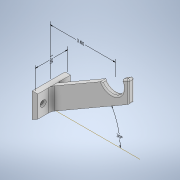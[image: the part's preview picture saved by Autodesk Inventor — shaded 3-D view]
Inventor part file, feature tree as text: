
AUTODESK INVENTOR PART (.ipt)
format: ipt  version: 2021.1 (Build 251245010, 245A)  size: 431,104 bytes
history: native  units: in
note: dims shown in document units (in); Inventor stores cm internally (conversion verified against a paired STEP export)
features: sketch x5, other x4, extrude x4, fillet x4, hole x1
ambient origin geometry x8: Origin, YZ Plane, XZ Plane, XY Plane, X Axis, Y Axis, Z Axis, Center Point
bodies: Solid2 (feature_tree)
feature tree (18):
  other  "Annotations"
  extrude  "Extrusion3"  Depth=0.25in
  extrude  "Extrusion4"  TaperAngle=30.0deg  [1 undecoded]
  sketch  "Sketch7"  dims[d26=1.075in d29=0.25in]
  extrude  "Extrusion5"  Depth=0.25in
  hole  "Hole3"  [1 undecoded]
  fillet  "Fillet3"  [1 undecoded]
  fillet  "Fillet4"  [1 undecoded]
  fillet  "Fillet5"  Radius=0.25in
  fillet  "Fillet6"  Radius=0.25in
  extrude  "Extrusion6"  Depth=0.0625in
  sketch  "Sketch5"  dims[d21=1.0in d22=0.25in]
  sketch  "Sketch6"  dims[d23=1.5in d24=0.0in d25=30.0deg]
  sketch  "Sketch8"  dims[d30=3.0in d31=0.25in d32=0.0in d33=0.0in d34=0.25in d35=0.25in]
  sketch  "Sketch9"  dims[d47=1.5in d48=0.0in d49=0.15in d50=0.75in d51=0.279in d52=0.25in d53=0.5635in d54=1.0in d55=0.8108in d65=0.0625in d66=0.0625in d67=0.0625in d68=0.125in d72=0.05in d73=0.0in d56=0.2085in d57=0.331in d58=1.5in d59=2.3174in d60=30.0deg d69=3.0in]
  other  "Linear Dimension 1"
  other  "Angular Dimension 1"
  other  "Linear Dimension 2"
note: 4 required parameter values undecoded (feature->parameter linkage not recoverable at this tier; creation-order binding heuristic only, values carry confidence <= 0.55)
